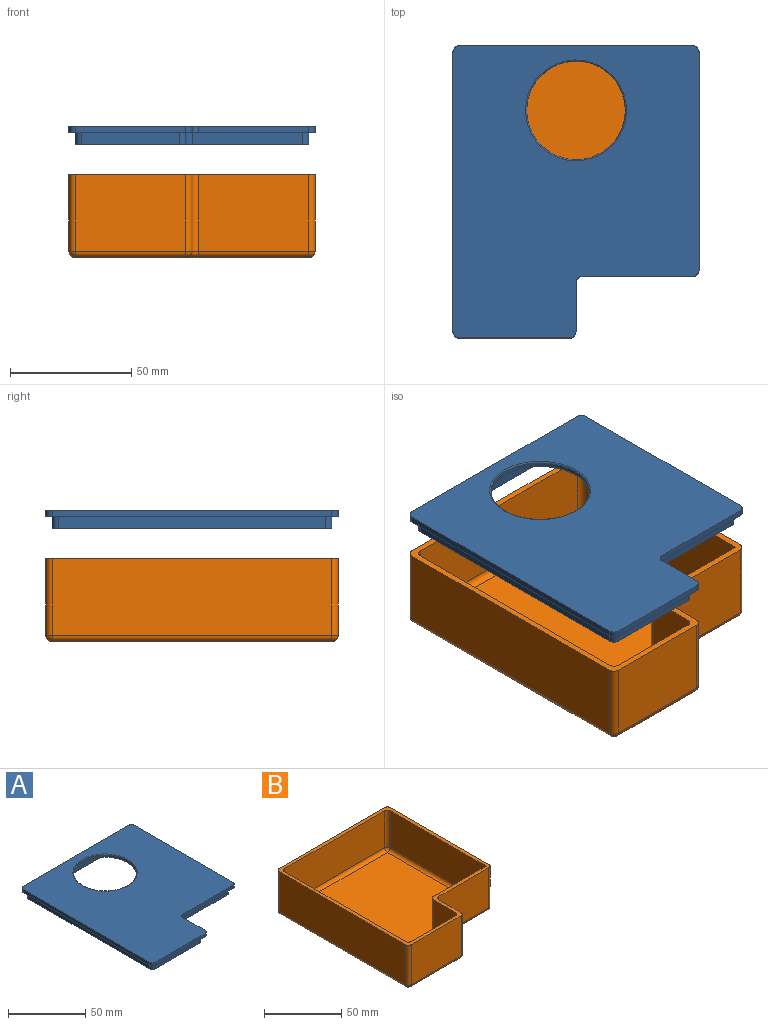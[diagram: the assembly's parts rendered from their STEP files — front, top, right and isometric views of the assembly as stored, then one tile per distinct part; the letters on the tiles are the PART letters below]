
ASSEMBLY  parts=2 mates=1
PART A: 43 faces, bbox 101.6x120.7x7.6 mm
  f0: plane 120.65x101.6mm, normal (0,0,-1), area 1103.2mm2, adj f1,f2,f3,f4,f5,f6,f8,f9
  f1: plane 96.52x2.54mm, normal (0,1,0), area 245.2mm2, adj f0,f7,f35,f40
  f2: plane 115.57x2.54mm, normal (-1,0,0), area 293.5mm2, adj f0,f7,f35,f36
  f3: plane 45.72x2.54mm, normal (0,-1,0), area 116.1mm2, adj f0,f7,f36,f37
  f4: plane 20.32x2.54mm, normal (1,0,0), area 51.6mm2, adj f0,f7,f37,f38
  f5: plane 45.72x2.54mm, normal (0,-1,0), area 116.1mm2, adj f0,f7,f38,f39
  f6: plane 90.17x2.54mm, normal (1,0,0), area 229mm2, adj f0,f7,f39,f40
  f7: plane 120.65x101.6mm, normal (0,0,1), area 9599.3mm2, adj f1,f2,f3,f4,f5,f6,f35,f36
  f8: plane 85.09x5.08mm, normal (1,0,0), area 432.3mm2, adj f0,f20,f29,f34
  f9: plane 45.72x5.08mm, normal (0,-1,0), area 232.3mm2, adj f0,f20,f29,f30
  f10: plane 20.32x5.08mm, normal (1,0,0), area 103.2mm2, adj f0,f20,f30,f31
  f11: plane 40.64x5.08mm, normal (0,-1,0), area 206.5mm2, adj f0,f20,f31,f32
  f12: plane 110.49x5.08mm, normal (-1,0,0), area 561.3mm2, adj f0,f20,f32,f33
  f13: plane 45.72x5.08mm, normal (0,1,0), area 232.3mm2, adj f20,f21,f23,f28
  f14: plane 80.01x5.08mm, normal (-1,0,0), area 406.5mm2, adj f20,f21,f23,f24
  f15: plane 86.36x5.08mm, normal (0,-1,0), area 438.7mm2, adj f20,f21,f24,f25
  f16: plane 105.41x5.08mm, normal (1,0,0), area 535.5mm2, adj f20,f21,f25,f26
  f17: plane 35.56x5.08mm, normal (0,1,0), area 180.6mm2, adj f20,f21,f26,f27
  f18: plane 20.32x5.08mm, normal (-1,0,0), area 103.2mm2, adj f20,f21,f27,f28
  f19: plane 91.44x5.08mm, normal (0,1,0), area 464.5mm2, adj f0,f20,f33,f34
  f20: plane 115.57x96.52mm, normal (0,0,-1), area 1051.6mm2, adj f8,f9,f10,f11,f12,f13,f14,f15
  f21: plane 110.49x91.44mm, normal (0,0,-1), area 7444.5mm2, adj f13,f14,f15,f16,f17,f18,f23,f24
  f22: cylinder r=20.32mm len=40.64mm, axis (0,0,1), area 194.6mm2, adj f41,f42
  f23: cylinder r=2.54mm len=5.08mm, axis (0,0,-1), area 20.3mm2, adj f13,f14,f20,f21
  f24: cylinder r=2.54mm len=5.08mm, axis (0,0,-1), area 20.3mm2, adj f14,f15,f20,f21
  f25: cylinder r=2.54mm len=5.08mm, axis (0,0,-1), area 20.3mm2, adj f15,f16,f20,f21
  f26: cylinder r=2.54mm len=5.08mm, axis (0,0,-1), area 20.3mm2, adj f16,f17,f20,f21
  f27: cylinder r=2.54mm len=5.08mm, axis (0,0,-1), area 20.3mm2, adj f17,f18,f20,f21
  f28: cylinder r=2.54mm len=5.08mm, axis (0,0,1), area 20.3mm2, adj f13,f18,f20,f21
  f29: cylinder r=2.54mm len=5.08mm, axis (0,0,1), area 20.3mm2, adj f0,f8,f9,f20
  f30: cylinder r=2.54mm len=5.08mm, axis (0,0,-1), area 20.3mm2, adj f0,f9,f10,f20
  f31: cylinder r=2.54mm len=5.08mm, axis (0,0,1), area 20.3mm2, adj f0,f10,f11,f20
  f32: cylinder r=2.54mm len=5.08mm, axis (0,0,1), area 20.3mm2, adj f0,f11,f12,f20
  f33: cylinder r=2.54mm len=5.08mm, axis (0,0,1), area 20.3mm2, adj f0,f12,f19,f20
  f34: cylinder r=2.54mm len=5.08mm, axis (0,0,1), area 20.3mm2, adj f0,f8,f19,f20
  f35: cylinder r=2.54mm len=2.54mm, axis (0,0,1), area 10.1mm2, adj f0,f1,f2,f7
  f36: cylinder r=2.54mm len=2.54mm, axis (0,0,-1), area 10.1mm2, adj f0,f2,f3,f7
  f37: cylinder r=2.54mm len=2.54mm, axis (0,0,1), area 10.1mm2, adj f0,f3,f4,f7
  f38: cylinder r=2.54mm len=2.54mm, axis (0,0,1), area 10.1mm2, adj f0,f4,f5,f7
  f39: cylinder r=2.54mm len=2.54mm, axis (0,0,-1), area 10.1mm2, adj f0,f5,f6,f7
  f40: cylinder r=2.54mm len=2.54mm, axis (0,0,-1), area 10.1mm2, adj f0,f1,f6,f7
  f41: torus R=20.83mm, axis (0,0,1), area 102.8mm2, adj f21,f22
  f42: torus R=20.83mm, axis (0,0,1), area 102.8mm2, adj f7,f22
PART B: 57 faces, bbox 101.6x120.7x34.3 mm
  f0: plane 96.52x31.75mm, normal (0,1,0), area 3064.5mm2, adj f6,f50,f54,f56
  f1: plane 115.57x31.75mm, normal (-1,0,0), area 3669.3mm2, adj f6,f47,f53,f56
  f2: plane 45.72x31.75mm, normal (0,-1,0), area 1451.6mm2, adj f6,f41,f47,f48
  f3: plane 31.75x20.32mm, normal (1,0,0), area 567.8mm2, adj f6,f15,f16,f17,f18,f19,f20,f21
  f4: plane 45.72x31.75mm, normal (0,-1,0), area 1451.6mm2, adj f6,f39,f43,f44
  f5: plane 90.17x31.75mm, normal (1,0,0), area 2862.9mm2, adj f6,f44,f49,f50
  f6: plane 120.65x101.6mm, normal (0,0,1), area 1101.8mm2, adj f0,f1,f2,f3,f4,f5,f8,f9
  f7: plane 115.57x96.52mm, normal (0,0,-1), area 9870mm2, adj f40,f42,f43,f48,f49,f53,f54
  f8: plane 29.21x20.32mm, normal (-1,0,0), area 516.1mm2, adj f6,f15,f16,f17,f18,f19,f20,f21
  f9: plane 48.26x29.21mm, normal (0,1,0), area 1409.7mm2, adj f6,f10,f36,f38
  f10: plane 87.63x29.21mm, normal (-1,0,0), area 2559.7mm2, adj f6,f9,f29,f34
  f11: plane 91.44x29.21mm, normal (0,-1,0), area 2671mm2, adj f6,f23,f28,f29
  f12: plane 110.49x29.21mm, normal (1,0,0), area 3227.4mm2, adj f6,f23,f24,f25
  f13: plane 40.64x29.21mm, normal (0,1,0), area 1187.1mm2, adj f6,f24,f30,f31
  f14: plane 110.49x91.44mm, normal (0,0,1), area 8818.4mm2, adj f25,f28,f31,f34,f35,f36,f37
  f15: plane 9.91x2.54mm, normal (0,0,1), area 25.2mm2, adj f3,f8,f19,f20
  f16: plane 7.37x2.54mm, normal (0,1,0), area 18.7mm2, adj f3,f8,f19,f21
  f17: plane 7.37x2.54mm, normal (0,-1,0), area 18.7mm2, adj f3,f8,f20,f22
  f18: plane 9.91x2.54mm, normal (0,0,-1), area 25.2mm2, adj f3,f8,f21,f22
  f19: cylinder r=0.13mm len=2.54mm, axis (-1,0,0), area 0.5mm2, adj f3,f8,f15,f16
  f20: cylinder r=0.13mm len=2.54mm, axis (1,0,0), area 0.5mm2, adj f3,f8,f15,f17
  f21: cylinder r=0.13mm len=2.54mm, axis (1,0,0), area 0.5mm2, adj f3,f8,f16,f18
  f22: cylinder r=0.13mm len=2.54mm, axis (-1,0,0), area 0.5mm2, adj f3,f8,f17,f18
  f23: cylinder r=2.54mm len=29.21mm, axis (0,0,-1), area 116.5mm2, adj f6,f11,f12,f26
  f24: cylinder r=2.54mm len=29.21mm, axis (0,0,-1), area 116.5mm2, adj f6,f12,f13,f27
  f25: cylinder r=2.54mm len=110.49mm, axis (0,-1,0), area 440.8mm2, adj f12,f14,f26,f27
  f26: sphere r=2.54mm, area 10.1mm2, adj f23,f25,f28
  f27: sphere r=2.54mm, area 10.1mm2, adj f24,f25,f31
  f28: cylinder r=2.54mm len=91.44mm, axis (-1,0,0), area 364.8mm2, adj f11,f14,f26,f32
  f29: cylinder r=2.54mm len=29.21mm, axis (0,0,-1), area 116.5mm2, adj f6,f10,f11,f32
  f30: cylinder r=2.54mm len=29.21mm, axis (0,0,-1), area 116.5mm2, adj f6,f8,f13,f33
  f31: cylinder r=2.54mm len=40.64mm, axis (1,0,0), area 162.1mm2, adj f13,f14,f27,f33
  f32: sphere r=2.54mm, area 10.1mm2, adj f28,f29,f34
  f33: sphere r=2.54mm, area 10.1mm2, adj f30,f31,f35
  f34: cylinder r=2.54mm len=87.63mm, axis (0,1,0), area 345.9mm2, adj f10,f14,f32,f36
  f35: cylinder r=2.54mm len=20.32mm, axis (0,1,0), area 81.1mm2, adj f8,f14,f33,f37
  f36: cylinder r=2.54mm len=48.26mm, axis (1,0,0), area 188.9mm2, adj f9,f14,f34,f37
  f37: torus R=5.08mm, axis (0,0,1), area 21.7mm2, adj f14,f35,f36,f38
  f38: cylinder r=2.54mm len=29.21mm, axis (0,0,1), area 116.5mm2, adj f6,f8,f9,f37
  f39: cylinder r=2.54mm len=31.75mm, axis (0,0,1), area 126.7mm2, adj f3,f4,f6,f40
  f40: torus R=5.08mm, axis (0,0,1), area 21.7mm2, adj f7,f39,f42,f43
  f41: cylinder r=2.54mm len=31.75mm, axis (0,0,1), area 126.7mm2, adj f2,f3,f6,f45
  f42: cylinder r=2.54mm len=20.32mm, axis (0,1,0), area 81.1mm2, adj f3,f7,f40,f45
  f43: cylinder r=2.54mm len=45.72mm, axis (1,0,0), area 182.4mm2, adj f4,f7,f40,f46
  f44: cylinder r=2.54mm len=31.75mm, axis (0,0,-1), area 126.7mm2, adj f4,f5,f6,f46
  f45: sphere r=2.54mm, area 10.1mm2, adj f41,f42,f48
  f46: sphere r=2.54mm, area 10.1mm2, adj f43,f44,f49
  f47: cylinder r=2.54mm len=31.75mm, axis (0,0,-1), area 126.7mm2, adj f1,f2,f6,f51
  f48: cylinder r=2.54mm len=45.72mm, axis (1,0,0), area 182.4mm2, adj f2,f7,f45,f51
  f49: cylinder r=2.54mm len=90.17mm, axis (0,1,0), area 359.8mm2, adj f5,f7,f46,f52
  f50: cylinder r=2.54mm len=31.75mm, axis (0,0,-1), area 126.7mm2, adj f0,f5,f6,f52
  f51: sphere r=2.54mm, area 10.1mm2, adj f47,f48,f53
  f52: sphere r=2.54mm, area 10.1mm2, adj f49,f50,f54
  f53: cylinder r=2.54mm len=115.57mm, axis (0,-1,0), area 461.1mm2, adj f1,f7,f51,f55
  f54: cylinder r=2.54mm len=96.52mm, axis (-1,0,0), area 385.1mm2, adj f0,f7,f52,f55
  f55: sphere r=2.54mm, area 10.1mm2, adj f53,f54,f56
  f56: cylinder r=2.54mm len=31.75mm, axis (0,0,1), area 126.7mm2, adj f0,f1,f6,f55
PLACE A t=(-37.89,-32.76,34.57)mm
PLACE B t=(0.19,0.21,-16.99)mm
MATE planar A.f6 <-> B.f5  axis (1,0,0) through (50.99,12.91,37.11)mm
